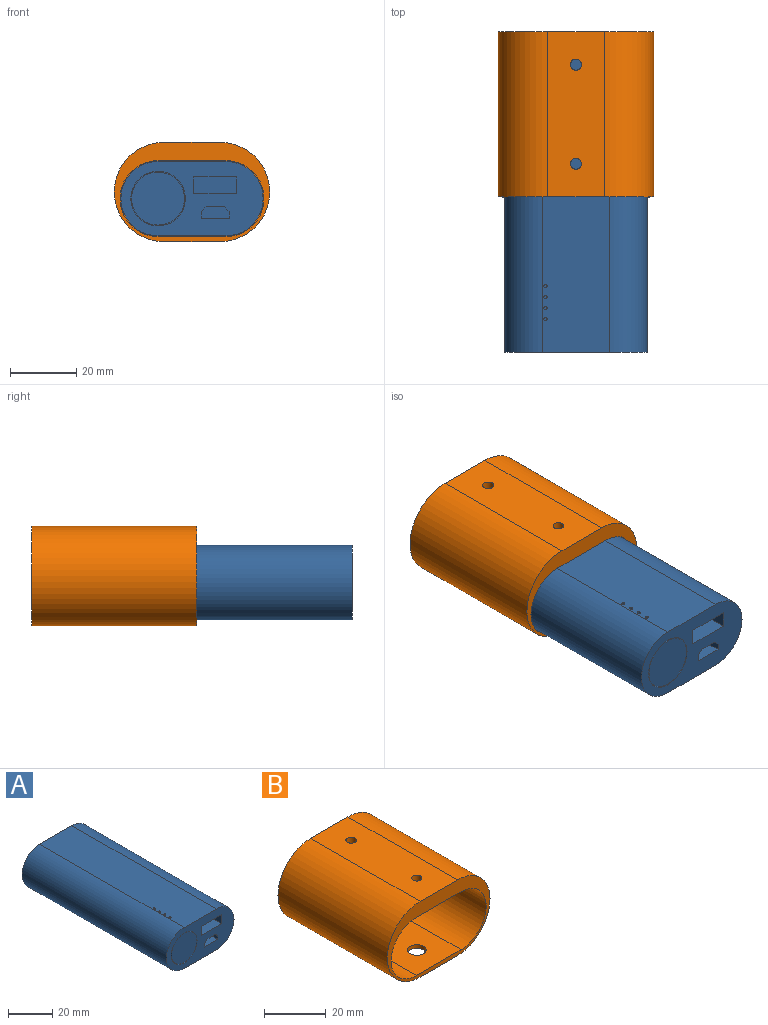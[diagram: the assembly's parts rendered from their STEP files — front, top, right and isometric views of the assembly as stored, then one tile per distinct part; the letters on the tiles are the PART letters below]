
ASSEMBLY  parts=2 mates=1
PART A: 30 faces, bbox 43x92x22.5 mm
  f0: plane 43x22.5mm, normal (0,-1,0), area 552.5mm2, adj f1,f2,f3,f4,f6,f10,f11,f12
  f1: cylinder r=11.25mm len=92mm, axis (0,-1,0), area 3251.5mm2, adj f0,f2,f4,f5
  f2: plane 92x20.5mm, normal (0,0,1), area 1882.9mm2, adj f0,f1,f3,f5,f22,f24,f26,f28
  f3: cylinder r=11.25mm len=92mm, axis (0,-1,0), area 3251.5mm2, adj f0,f2,f4,f5
  f4: plane 92x20.5mm, normal (0,0,-1), area 1886mm2, adj f0,f1,f3,f5
  f5: plane 43x22.5mm, normal (0,1,0), area 858.9mm2, adj f1,f2,f3,f4
  f6: cylinder r=8.25mm len=16.5mm, axis (0,-1,0), area 259.2mm2, adj f0,f7
  f7: plane 16.5x16.5mm, normal (0,-1,0), area 12.8mm2, adj f6,f8
  f8: cylinder r=8mm len=16mm, axis (0,1,0), area 251.3mm2, adj f7,f9
  f9: plane 16x16mm, normal (0,-1,0), area 201.1mm2, adj f8
  f10: plane 25x8.5mm, normal (0,0,1), area 212.5mm2, adj f0,f11,f15,f16
  f11: plane 25x2mm, normal (-1,0,0), area 50mm2, adj f0,f10,f12,f16
  f12: plane 25x1.5mm, normal (-0.71,0,-0.71), area 53mm2, adj f0,f11,f13,f16
  f13: plane 25x5.5mm, normal (0,0,-1), area 137.5mm2, adj f0,f12,f14,f16
  f14: plane 25x1.5mm, normal (0.71,0,-0.71), area 53mm2, adj f0,f13,f15,f16
  f15: plane 25x2mm, normal (1,0,0), area 50mm2, adj f0,f10,f14,f16
  f16: plane 8.5x3.5mm, normal (0,-1,0), area 27.5mm2, adj f10,f11,f12,f13,f14,f15
  f17: plane 25x5mm, normal (1,0,0), area 125mm2, adj f0,f18,f20,f21
  f18: plane 25x13mm, normal (0,0,1), area 325mm2, adj f0,f17,f19,f21
  f19: plane 25x5mm, normal (-1,0,0), area 125mm2, adj f0,f18,f20,f21
  f20: plane 25x13mm, normal (0,0,-1), area 325mm2, adj f0,f17,f19,f21
  f21: plane 13x5mm, normal (0,-1,0), area 65mm2, adj f17,f18,f19,f20
  f22: cylinder r=0.5mm len=2mm, axis (0,0,1), area 6.3mm2, adj f2,f23
  f23: plane 1x1mm, normal (0,0,1), area 0.8mm2, adj f22
  f24: cylinder r=0.5mm len=2mm, axis (0,0,1), area 6.3mm2, adj f2,f25
  f25: plane 1x1mm, normal (0,0,1), area 0.8mm2, adj f24
  f26: cylinder r=0.5mm len=2mm, axis (0,0,1), area 6.3mm2, adj f2,f27
  f27: plane 1x1mm, normal (0,0,1), area 0.8mm2, adj f26
  f28: cylinder r=0.5mm len=2mm, axis (0,0,1), area 6.3mm2, adj f2,f29
  f29: plane 1x1mm, normal (0,0,1), area 0.8mm2, adj f28
PART B: 26 faces, bbox 47x50x30 mm
  f0: plane 47x30mm, normal (0,1,0), area 1121.2mm2, adj f2,f3,f4,f5,f11,f16,f17
  f1: plane 43.5x23mm, normal (0,-1,0), area 751.9mm2, adj f7,f8,f9,f10,f11,f12,f14
  f2: cylinder r=15mm len=50mm, axis (0,1,0), area 2356.2mm2, adj f0,f3,f5,f6
  f3: plane 50x17mm, normal (0,0,1), area 832.4mm2, adj f0,f2,f4,f6,f24,f25
  f4: cylinder r=15mm len=50mm, axis (0,1,0), area 2356.2mm2, adj f0,f3,f5,f6
  f5: plane 50x17mm, normal (0,0,-1), area 793.5mm2, adj f0,f2,f4,f6,f22,f23
  f6: plane 47x30mm, normal (0,-1,0), area 329.9mm2, adj f2,f3,f4,f5,f7,f8,f9,f10
  f7: cylinder r=11.5mm len=45mm, axis (0,-1,0), area 1625.8mm2, adj f1,f6,f8,f10
  f8: plane 45x20.5mm, normal (0,0,1), area 866mm2, adj f1,f6,f7,f9,f22,f23
  f9: cylinder r=11.5mm len=45mm, axis (0,-1,0), area 1625.8mm2, adj f1,f6,f8,f10
  f10: plane 45x20.5mm, normal (0,0,-1), area 866mm2, adj f1,f6,f7,f9,f18,f20
  f11: cylinder r=5mm len=10mm, axis (0,-1,0), area 157.1mm2, adj f0,f1
  f12: cylinder r=3mm len=6mm, axis (0,-1,0), area 56.5mm2, adj f1,f13
  f13: plane 6x6mm, normal (0,-1,0), area 19.7mm2, adj f12,f16
  f14: cylinder r=3mm len=6mm, axis (0,-1,0), area 56.5mm2, adj f1,f15
  f15: plane 6x6mm, normal (0,-1,0), area 19.7mm2, adj f14,f17
  f16: cylinder r=1.65mm len=3.3mm, axis (0,-1,0), area 20.7mm2, adj f0,f13
  f17: cylinder r=1.65mm len=3.3mm, axis (0,-1,0), area 20.7mm2, adj f0,f15
  f18: cylinder r=3mm len=6mm, axis (0,0,-1), area 56.5mm2, adj f10,f19
  f19: plane 6x6mm, normal (0,0,-1), area 19.2mm2, adj f18,f25
  f20: cylinder r=3mm len=6mm, axis (0,0,-1), area 56.5mm2, adj f10,f21
  f21: plane 6x6mm, normal (0,0,-1), area 19.7mm2, adj f20,f24
  f22: cylinder r=3mm len=6mm, axis (0,0,-1), area 28.3mm2, adj f5,f8
  f23: cylinder r=3mm len=6mm, axis (0,0,-1), area 28.3mm2, adj f5,f8
  f24: cylinder r=1.65mm len=3.3mm, axis (0,0,-1), area 25.9mm2, adj f3,f21
  f25: cylinder r=1.7mm len=3.4mm, axis (0,0,-1), area 26.7mm2, adj f3,f19
PLACE A t=(-0.46,19.99,0)mm
PLACE B t=(-0.46,116.99,0)mm
MATE planar A.f1 <-> B.f7  axis (0,1,0) through (9.79,111.99,0)mm
